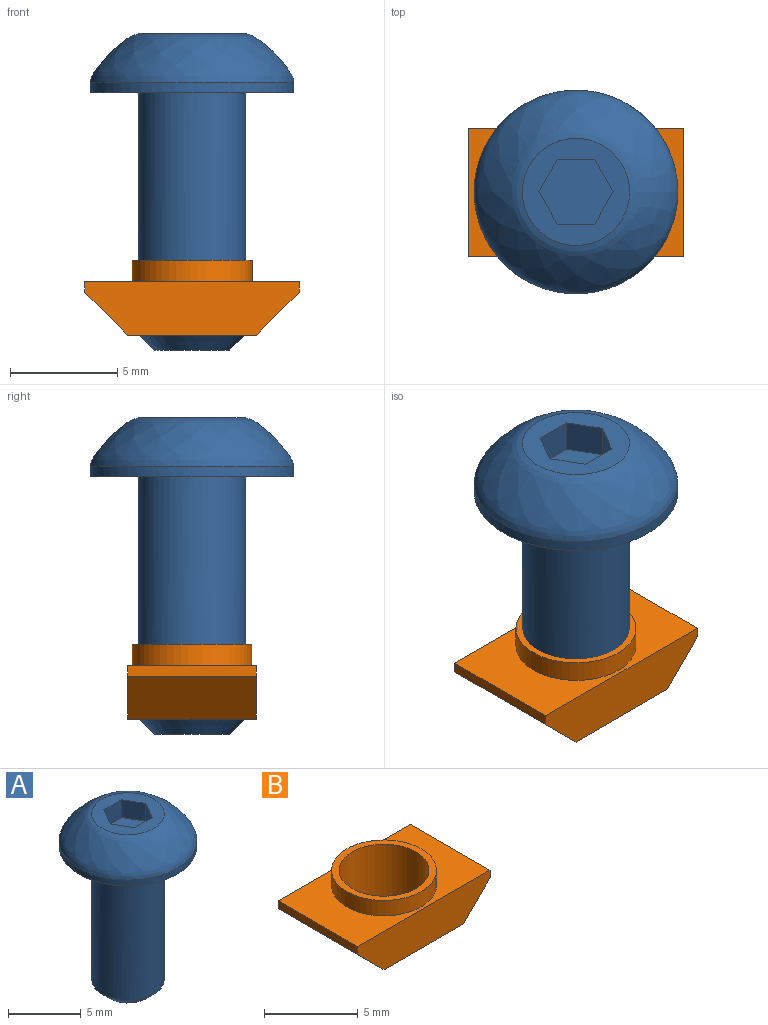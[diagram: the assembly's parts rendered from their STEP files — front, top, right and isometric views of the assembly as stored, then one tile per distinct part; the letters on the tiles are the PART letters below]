
ASSEMBLY  parts=2 mates=1
PART A: 14 faces, bbox 9.5x9.5x14.8 mm
  f0: plane 5.01x5.01mm, normal (0,0,1), area 11.8mm2, adj f3,f4,f5,f6,f7,f8,f10
  f1: cylinder r=4.75mm len=9.5mm, axis (0,0,-1), area 14.9mm2, adj f2,f10
  f2: plane 9.5x9.5mm, normal (0,0,-1), area 51.2mm2, adj f1,f11
  f3: plane 1.5x1.5mm, normal (-0.87,-0.5,0), area 2.6mm2, adj f0,f4,f8,f9
  f4: plane 1.73x1.5mm, normal (0,-1,0), area 2.6mm2, adj f0,f3,f5,f9
  f5: plane 1.5x1.5mm, normal (0.87,-0.5,0), area 2.6mm2, adj f0,f4,f6,f9
  f6: plane 1.5x1.5mm, normal (0.87,0.5,0), area 2.6mm2, adj f0,f5,f7,f9
  f7: plane 1.73x1.5mm, normal (0,1,0), area 2.6mm2, adj f0,f6,f8,f9
  f8: plane 1.5x1.5mm, normal (-0.87,0.5,0), area 2.6mm2, adj f0,f3,f7,f9
  f9: plane 3.46x3mm, normal (0,0,1), area 7.8mm2, adj f3,f4,f5,f6,f7,f8
  f10: bspline ~9.5x9.5mm, area 78.3mm2, adj f0,f1
  f11: cylinder r=2.5mm len=11.25mm, axis (0,0,1), area 176.7mm2, adj f2,f13
  f12: plane 3.5x3.5mm, normal (0,0,-1), area 9.6mm2, adj f13
  f13: cone r=1.75mm half-angle=45deg, axis (0,0,1), area 14.2mm2, adj f11,f12
PART B: 11 faces, bbox 10x6x3.5 mm
  f0: plane 10x2.5mm, normal (0,-1,0), area 21mm2, adj f1,f4,f5,f6,f9,f10
  f1: plane 6x0.5mm, normal (1,0,0), area 3mm2, adj f0,f2,f5,f10
  f2: plane 10x2.5mm, normal (0,1,0), area 21mm2, adj f1,f4,f5,f6,f9,f10
  f3: cylinder r=2.4mm len=4.8mm, axis (0,0,-1), area 52.8mm2, adj f6,f8
  f4: plane 6x0.5mm, normal (-1,0,0), area 3mm2, adj f0,f2,f5,f9
  f5: plane 10x6mm, normal (0,0,1), area 35.4mm2, adj f0,f1,f2,f4,f7
  f6: plane 6x6mm, normal (0,0,-1), area 17.9mm2, adj f0,f2,f3,f9,f10
  f7: cylinder r=2.8mm len=5.6mm, axis (0,0,-1), area 17.6mm2, adj f5,f8
  f8: plane 5.6x5.6mm, normal (0,0,1), area 6.5mm2, adj f3,f7
  f9: plane 6x2mm, normal (-0.71,0,-0.71), area 17mm2, adj f0,f2,f4,f6
  f10: plane 6x2mm, normal (0.71,0,-0.71), area 17mm2, adj f0,f1,f2,f6
PLACE A at identity
PLACE B t=(-12.5,0,-11.3)mm
MATE fastened B.f3 <-> A.f1  axis (0,0,1) through (-12.5,0,-8.8)mm
